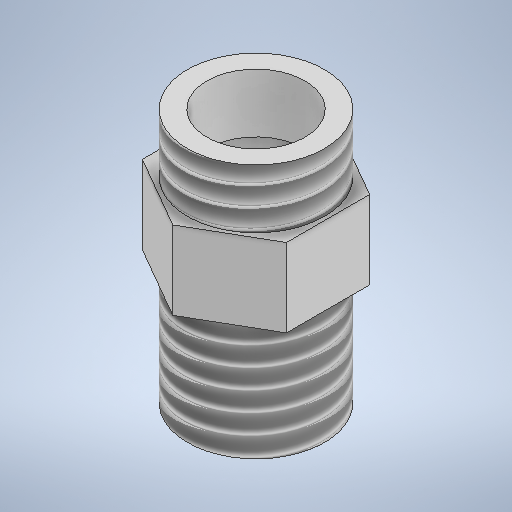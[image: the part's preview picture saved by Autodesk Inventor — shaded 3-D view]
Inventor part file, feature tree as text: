
AUTODESK INVENTOR PART (.ipt)
format: ipt  version: 2025.1 (Build 291241000, 241)  size: 309,248 bytes
history: native  units: mm
features: sketch x5, extrude x3, hole x2, thread x2
ambient origin geometry x8: Origin, YZ Plane, XZ Plane, XY Plane, X Axis, Y Axis, Z Axis, Center Point
bodies: Solid1 (feature_tree)
feature tree (12):
  extrude  "Extrusion1"  Depth=4.0mm TaperAngle=0.0deg
  extrude  "Extrusion2"  Depth=3.0mm TaperAngle=0.0deg
  extrude  "Extrusion3"  Depth=6.0mm TaperAngle=0.0deg
  hole  "Hole1"  [1 undecoded]
  thread  "Thread1"  [1 undecoded]
  thread  "Thread2"  [1 undecoded]
  hole  "Hole2"  [1 undecoded]
  sketch  "Sketch2"  dims[d0=8.5mm d1=4.0mm d2=0.0mm]
  sketch  "Sketch3"  dims[d3=7.0mm d4=3.0mm d5=0.0mm]
  sketch  "Sketch4"  dims[d6=7.0mm d7=6.0mm d8=0.0mm]
  sketch  "Sketch5"  dims[d9=5.0mm d10=5.0mm d11=4.0mm d12=2.0mm d13=90.0deg d14=8.0mm d15=0.0mm d16=35.9mm d17=0.0mm d18=35.9mm d19=0.0mm]
  sketch  "Sketch6"  dims[d20=6.0mm d21=6.0mm d22=4.0mm d23=2.0mm d24=90.0deg d25=8.0mm d26=0.0mm]
note: 4 required parameter values undecoded (feature->parameter linkage not recoverable at this tier; creation-order binding heuristic only, values carry confidence <= 0.55)
